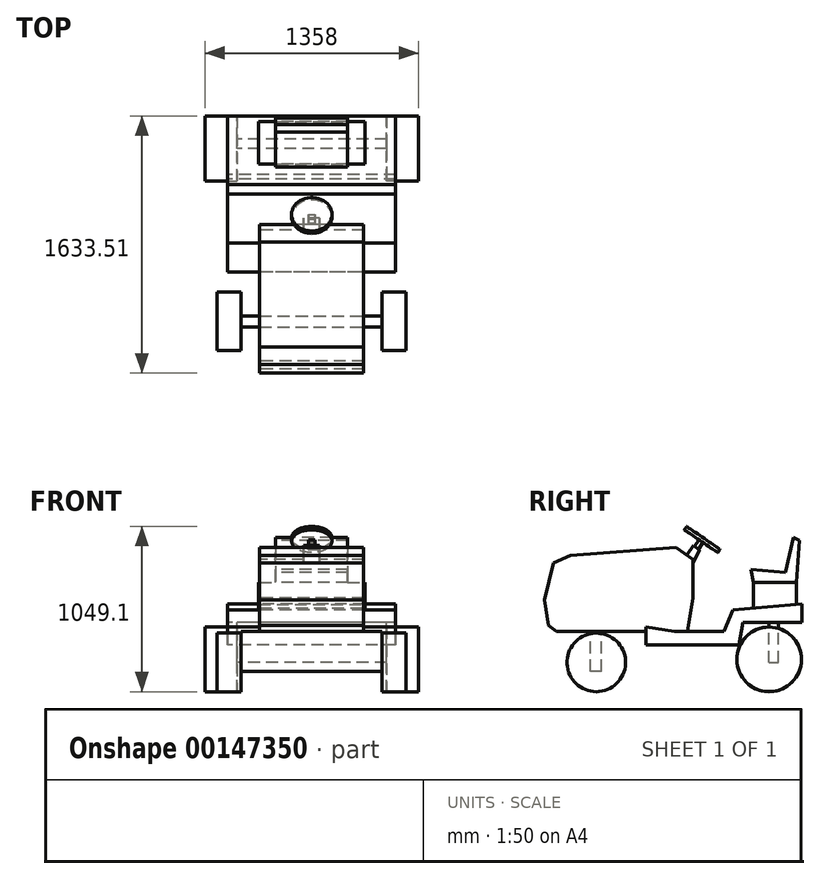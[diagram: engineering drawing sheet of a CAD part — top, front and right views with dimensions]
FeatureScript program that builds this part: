
annotation { "Feature Type Name" : "Feature", "Feature Type Description" : "" }
export const myFeature = defineFeature(function(context is Context, id is Id, definition is map)
    precondition{}
    {
        {
            var Q0;
            Q0=qCreatedBy(makeId("Top.planeOp"),FACE);
            var sketch = newSketch(context, id + "F0", { "sketchPlane" : qUnion([Q0])});
            skLineSegment(sketch, "E0.bottom", {"start": v(-684.79, 956.16) * mm, "end": v(686.81, 956.16) * mm});
            skLineSegment(sketch, "E0.top", {"start": v(-684.79, -771.04) * mm, "end": v(686.81, -771.04) * mm});
            skLineSegment(sketch, "E0.left", {"start": v(-684.79, 956.16) * mm, "end": v(-684.79, -771.04) * mm});
            skLineSegment(sketch, "E0.right", {"start": v(686.81, 956.16) * mm, "end": v(686.81, -771.04) * mm});
            skSolve(sketch);
        }
        {
            var Q0;
            Q0=qCreatedBy(makeId("Right.planeOp"),FACE);
            var sketch = newSketch(context, id + "F1", { "sketchPlane" : qUnion([Q0])});
            skLineSegment(sketch, "E1.bottom", {"start": v(954.63, 0) * mm, "end": v(-771.04, 0) * mm});
            skLineSegment(sketch, "E1.top", {"start": v(954.63, 1041.4) * mm, "end": v(-771.04, 1041.4) * mm});
            skLineSegment(sketch, "E1.left", {"start": v(954.63, 0) * mm, "end": v(954.63, 1041.4) * mm});
            skLineSegment(sketch, "E1.right", {"start": v(-771.04, 0) * mm, "end": v(-771.04, 1041.4) * mm});
            skSolve(sketch);
        }
        {
            var Q0;
            Q0=makeQuery(id+"F1.imprint","IMPRINT",FACE,{"disambiguationData":[TD([[makeQuery(id+"F1.imprint","IMPRINT",EDGE,{"derivedFrom":sQuery(id+"F1.wireOp",EDGE,"E1.bottom")}),-1.0]])]});
            var sketch = newSketch(context, id + "F2", { "sketchPlane" : qUnion([Q0])});
            skLineSegment(sketch, "E2.0", {"start": v(954.63, 438.64) * mm, "end": v(954.63, 557.7) * mm});
            skLineSegment(sketch, "E3", {"start": v(954.63, 557.7) * mm, "end": v(517.3, 520.7) * mm});
            skPoint(sketch, "E3.endSnap0", {"position": v(954.63, 520.7) * mm});
            skLineSegment(sketch, "E4", {"start": v(517.3, 520.7) * mm, "end": v(458.98, 382.76) * mm});
            skLineSegment(sketch, "E5", {"start": v(458.98, 382.76) * mm, "end": v(145.54, 382.76) * mm});
            skLineSegment(sketch, "E6", {"start": v(145.54, 382.76) * mm, "end": v(-36.7, 411.92) * mm});
            skLineSegment(sketch, "E7", {"start": v(-36.7, 411.92) * mm, "end": v(-36.7, 297.72) * mm});
            skLineSegment(sketch, "E8", {"start": v(-36.7, 297.72) * mm, "end": v(553.74, 297.72) * mm});
            skLineSegment(sketch, "E9", {"start": v(553.74, 297.72) * mm, "end": v(580.47, 438.64) * mm});
            skLineSegment(sketch, "E10", {"start": v(580.47, 438.64) * mm, "end": v(954.63, 438.64) * mm});
            skPoint(sketch, "E11.orphan", {"position": v(954.63, 1041.4) * mm});
            skPoint(sketch, "E12.0.end.orphan", {"position": v(-771.04, 1041.4) * mm});
            skPoint(sketch, "E13.0.start.orphan", {"position": v(-771.04, 0) * mm});
            skPoint(sketch, "E14.0.start.orphan", {"position": v(954.63, 0) * mm});
            skSolve(sketch);
        }
        {
            var Q0;
            Q0=qSketchRegion(id+"F2",true);
            extrude(context, id + "F3", {"entities" : qUnion([Q0]), "endBound" : BoundingType.SYMMETRIC, "depth" : 1066.8 * mm});
        }
        {
            var Q0;
            Q0=makeQuery(id+"F1.imprint","IMPRINT",FACE,{"disambiguationData":[TD([[makeQuery(id+"F1.imprint","IMPRINT",EDGE,{"derivedFrom":sQuery(id+"F1.wireOp",EDGE,"E1.bottom")}),-1.0]])]});
            var sketch = newSketch(context, id + "F4", { "sketchPlane" : qUnion([Q0])});
            skLineSegment(sketch, "E15.0", {"start": v(458.98, 382.76) * mm, "end": v(145.54, 382.76) * mm});
            skLineSegment(sketch, "E16", {"start": v(228.74, 382.76) * mm, "end": v(262.65, 594.7) * mm});
            skLineSegment(sketch, "E17", {"start": v(262.65, 594.7) * mm, "end": v(262.65, 840.83) * mm});
            skLineSegment(sketch, "E18", {"start": v(262.65, 840.83) * mm, "end": v(154.41, 914.7) * mm});
            skLineSegment(sketch, "E19", {"start": v(154.41, 914.7) * mm, "end": v(-513.94, 864.88) * mm});
            skLineSegment(sketch, "E20", {"start": v(-513.94, 864.88) * mm, "end": v(-623.9, 818.5) * mm});
            skLineSegment(sketch, "E21", {"start": v(-623.9, 818.5) * mm, "end": v(-678.88, 583.11) * mm});
            skLineSegment(sketch, "E22", {"start": v(-678.88, 583.11) * mm, "end": v(-653.1, 419.89) * mm});
            skLineSegment(sketch, "E23", {"start": v(228.74, 382.76) * mm, "end": v(-603.28, 382.76) * mm});
            skLineSegment(sketch, "E24", {"start": v(-603.28, 382.76) * mm, "end": v(-653.1, 419.89) * mm});
            skPoint(sketch, "E25.0.end.orphan", {"position": v(553.74, 297.72) * mm});
            skPoint(sketch, "E25.0.start.orphan", {"position": v(-36.7, 297.72) * mm});
            skPoint(sketch, "E26.0.end.orphan", {"position": v(-36.7, 411.92) * mm});
            skSolve(sketch);
        }
        {
            var Q0;
            Q0=qSketchRegion(id+"F4",true);
            extrude(context, id + "F5", {"entities" : qUnion([Q0]), "operationType" : NewBodyOperationType.ADD, "endBound" : BoundingType.SYMMETRIC, "depth" : 660.4 * mm});
        }
        {
            var Q0;
            Q0=makeQuery(id+"F5.opExtrude","SWEPT_FACE",FACE,{"disambiguationData":[OSD([sQuery(id+"F4.wireOp",EDGE,"E23")])]});
            var sketch = newSketch(context, id + "F6", { "sketchPlane" : qUnion([Q0])});
            skLineSegment(sketch, "E27.rect.bottom", {"start": v(-447.73, 317.68) * mm, "end": v(447.73, 317.68) * mm});
            skLineSegment(sketch, "E27.rect.top", {"start": v(-447.73, 386.72) * mm, "end": v(447.73, 386.72) * mm});
            skLineSegment(sketch, "E27.rect.left", {"start": v(-447.73, 317.68) * mm, "end": v(-447.73, 386.72) * mm});
            skLineSegment(sketch, "E27.rect.right", {"start": v(447.73, 317.68) * mm, "end": v(447.73, 386.72) * mm});
            skPoint(sketch, "E27.rect.middle", {"position": v(0, 352.2) * mm});
            skSolve(sketch);
        }
        {
            var Q0;
            Q0=qSketchRegion(id+"F6",true);
            extrude(context, id + "F7", {"entities" : qUnion([Q0]), "operationType" : NewBodyOperationType.ADD, "depth" : 254 * mm});
        }
        {
            var Q0;
            Q0=makeQuery(id+"F7.opExtrude","SWEPT_FACE",FACE,{"disambiguationData":[OSD([sQuery(id+"F6.wireOp",EDGE,"E27.rect.left")])]});
            var sketch = newSketch(context, id + "F8", { "sketchPlane" : qUnion([Q0])});
            skLineSegment(sketch, "E28.0", {"start": v(-954.63, 0) * mm, "end": v(771.04, 0) * mm});
            skCircle(sketch, "E29", {"center": v(350.72, 186.22) * mm, "radius": 186.22 * mm});
            skSolve(sketch);
        }
        {
            var Q0;
            Q0=qSketchRegion(id+"F8",true);
            extrude(context, id + "F9", {"entities" : qUnion([Q0]), "depth" : 152.4 * mm});
        }
        {
            var Q0;
            Q0=makeQuery(id+"F9.opExtrude","SWEPT_BODY",BODY,{"disambiguationData":[OSD([sQuery(id+"F8.wireOp",EDGE,"E29")])]});
            var Q1;
            Q1=makeQuery(id+"F1.imprint","IMPRINT",FACE,{"disambiguationData":[TD([[makeQuery(id+"F1.imprint","IMPRINT",EDGE,{"derivedFrom":sQuery(id+"F1.wireOp",EDGE,"E1.bottom")}),-1.0]])]});
            mirror(context, id + "F10", {"operationType" : NewBodyOperationType.ADD, "entities" : qUnion([Q0]), "mirrorPlane" : qUnion([Q1])});
        }
        {
            var Q0;
            Q0=makeQuery(id+"F3.opExtrude","SWEPT_FACE",FACE,{"disambiguationData":[OSD([sQuery(id+"F2.wireOp",EDGE,"E10")])]});
            var sketch = newSketch(context, id + "F11", { "sketchPlane" : qUnion([Q0])});
            skLineSegment(sketch, "E30.rect.bottom", {"start": v(475.8, -747.09) * mm, "end": v(-475.8, -747.09) * mm});
            skLineSegment(sketch, "E30.rect.top", {"start": v(475.8, -805.5) * mm, "end": v(-475.8, -805.5) * mm});
            skLineSegment(sketch, "E30.rect.left", {"start": v(475.8, -747.09) * mm, "end": v(475.8, -805.5) * mm});
            skLineSegment(sketch, "E30.rect.right", {"start": v(-475.8, -747.09) * mm, "end": v(-475.8, -805.5) * mm});
            skPoint(sketch, "E30.rect.middle", {"position": v(0, -776.3) * mm});
            skPoint(sketch, "E31.orphan", {"position": v(0, -954.63) * mm});
            skSolve(sketch);
        }
        {
            var Q0;
            Q0=qSketchRegion(id+"F11",true);
            extrude(context, id + "F12", {"entities" : qUnion([Q0]), "operationType" : NewBodyOperationType.ADD, "depth" : 254 * mm});
        }
        {
            var Q0;
            Q0=makeQuery(id+"F12.opExtrude","SWEPT_FACE",FACE,{"disambiguationData":[OSD([sQuery(id+"F11.wireOp",EDGE,"E30.rect.right")])]});
            var sketch = newSketch(context, id + "F13", { "sketchPlane" : qUnion([Q0])});
            skCircle(sketch, "E32", {"center": v(-747.09, 205.12) * mm, "radius": 205.12 * mm});
            skPoint(sketch, "E32.centerSnap0", {"position": v(-747.09, 184.64) * mm});
            skSolve(sketch);
        }
        {
            var Q0;
            Q0=qSketchRegion(id+"F13",true);
            extrude(context, id + "F14", {"entities" : qUnion([Q0]), "operationType" : NewBodyOperationType.ADD, "depth" : 203.2 * mm});
        }
        {
            var Q0;
            Q0=makeQuery(id+"F12.opExtrude","SWEPT_FACE",FACE,{"disambiguationData":[OSD([sQuery(id+"F11.wireOp",EDGE,"E30.rect.left")])]});
            var sketch = newSketch(context, id + "F15", { "sketchPlane" : qUnion([Q0])});
            skCircle(sketch, "E33", {"center": v(747.09, 205.12) * mm, "radius": 205.12 * mm});
            skArc(sketch, "E34.0", {"start": v(805.5, 401.75) * mm, "mid": v(717.57, 2.13) * mm, "end": v(747.09, 410.25) * mm});
            skSolve(sketch);
        }
        {
            var Q0;
            Q0=qSketchRegion(id+"F15",true);
            extrude(context, id + "F16", {"entities" : qUnion([Q0]), "operationType" : NewBodyOperationType.ADD, "depth" : 203.2 * mm});
        }
        {
            var Q0;
            Q0=makeQuery(id+"F3.opExtrude","SWEPT_FACE",FACE,{"disambiguationData":[OSD([sQuery(id+"F2.wireOp",EDGE,"E10")])]});
            var sketch = newSketch(context, id + "F17", { "sketchPlane" : qUnion([Q0])});
            skLineSegment(sketch, "E35.rect.bottom", {"start": v(-336.71, -648.84) * mm, "end": v(336.71, -648.84) * mm});
            skLineSegment(sketch, "E35.rect.top", {"start": v(-336.71, -919.68) * mm, "end": v(336.71, -919.68) * mm});
            skLineSegment(sketch, "E35.rect.left", {"start": v(-336.71, -648.84) * mm, "end": v(-336.71, -919.68) * mm});
            skLineSegment(sketch, "E35.rect.right", {"start": v(336.71, -648.84) * mm, "end": v(336.71, -919.68) * mm});
            skPoint(sketch, "E35.rect.middle", {"position": v(0, -784.26) * mm});
            skPoint(sketch, "E35.rect.middle.positionSnap0", {"position": v(0, -747.09) * mm});
            skPoint(sketch, "E35.rect.centerSnap0", {"position": v(0, -747.09) * mm});
            skSolve(sketch);
        }
        {
            var Q0;
            Q0=qSketchRegion(id+"F17",true);
            extrude(context, id + "F18", {"entities" : qUnion([Q0]), "operationType" : NewBodyOperationType.ADD, "oppositeDirection" : true, "depth" : 254 * mm});
        }
        {
            var Q0;
            Q0=makeQuery(id+"F1.imprint","IMPRINT",FACE,{"disambiguationData":[TD([[makeQuery(id+"F1.imprint","IMPRINT",EDGE,{"derivedFrom":sQuery(id+"F1.wireOp",EDGE,"E1.bottom")}),-1.0]])]});
            var sketch = newSketch(context, id + "F19", { "sketchPlane" : qUnion([Q0])});
            skLineSegment(sketch, "E36.0", {"start": v(648.84, 692.64) * mm, "end": v(919.68, 692.64) * mm});
            skLineSegment(sketch, "E37", {"start": v(919.68, 692.64) * mm, "end": v(939.6, 959.61) * mm});
            skLineSegment(sketch, "E38", {"start": v(939.6, 959.61) * mm, "end": v(900.08, 978.5) * mm});
            skLineSegment(sketch, "E39", {"start": v(900.08, 978.5) * mm, "end": v(850.25, 758.59) * mm});
            skLineSegment(sketch, "E40", {"start": v(850.25, 758.59) * mm, "end": v(630.33, 775.77) * mm});
            skLineSegment(sketch, "E41", {"start": v(630.33, 775.77) * mm, "end": v(648.84, 692.64) * mm});
            skSolve(sketch);
        }
        {
            var Q0;
            Q0=qSketchRegion(id+"F19",true);
            extrude(context, id + "F20", {"entities" : qUnion([Q0]), "operationType" : NewBodyOperationType.ADD, "endBound" : BoundingType.SYMMETRIC, "depth" : 457.2 * mm});
        }
        {
            var Q0;
            Q0=makeQuery(id+"F1.imprint","IMPRINT",FACE,{"disambiguationData":[TD([[makeQuery(id+"F1.imprint","IMPRINT",EDGE,{"derivedFrom":sQuery(id+"F1.wireOp",EDGE,"E1.bottom")}),-1.0]])]});
            var sketch = newSketch(context, id + "F21", { "sketchPlane" : qUnion([Q0])});
            skLineSegment(sketch, "E42.0", {"start": v(262.65, 840.83) * mm, "end": v(224.07, 867.17) * mm});
            skLineSegment(sketch, "E43.0", {"start": v(262.65, 813.34) * mm, "end": v(262.65, 840.83) * mm});
            skLineSegment(sketch, "E44", {"start": v(224.07, 867.17) * mm, "end": v(265.45, 927.8) * mm});
            skLineSegment(sketch, "E45", {"start": v(265.45, 927.8) * mm, "end": v(304.6, 901.08) * mm});
            skLineSegment(sketch, "E46", {"start": v(304.6, 901.08) * mm, "end": v(262.65, 813.34) * mm});
            skPoint(sketch, "E47.orphan", {"position": v(262.65, 594.7) * mm});
            skPoint(sketch, "E48.orphan", {"position": v(154.41, 914.7) * mm});
            skSolve(sketch);
        }
        {
            var Q0;
            Q0=qSketchRegion(id+"F21",true);
            extrude(context, id + "F22", {"entities" : qUnion([Q0]), "operationType" : NewBodyOperationType.ADD, "endBound" : BoundingType.SYMMETRIC, "depth" : 101.6 * mm});
        }
        {
            var Q0;
            Q0=makeQuery(id+"F22.opExtrude","SWEPT_FACE",FACE,{"disambiguationData":[OSD([sQuery(id+"F21.wireOp",EDGE,"E45")])]});
            var sketch = newSketch(context, id + "F23", { "sketchPlane" : qUnion([Q0])});
            skLineSegment(sketch, "E49.rect.bottom", {"start": v(-19.95, -294.88) * mm, "end": v(19.95, -294.88) * mm});
            skLineSegment(sketch, "E49.rect.top", {"start": v(-19.95, -262.9) * mm, "end": v(19.95, -262.9) * mm});
            skLineSegment(sketch, "E49.rect.left", {"start": v(-19.95, -294.88) * mm, "end": v(-19.95, -262.9) * mm});
            skLineSegment(sketch, "E49.rect.right", {"start": v(19.95, -294.88) * mm, "end": v(19.95, -262.9) * mm});
            skPoint(sketch, "E49.rect.middle", {"position": v(0, -278.9) * mm});
            skSolve(sketch);
        }
        {
            var Q0;
            Q0=qSketchRegion(id+"F23",true);
            extrude(context, id + "F24", {"entities" : qUnion([Q0]), "operationType" : NewBodyOperationType.ADD, "depth" : 50.8 * mm});
        }
        {
            var Q0;
            Q0=makeQuery(id+"F24.opExtrude","CAP_FACE",FACE,{"disambiguationData":[OSD([sQuery(id+"F23.wireOp",EDGE,"E49.rect.bottom"),sQuery(id+"F23.wireOp",EDGE,"E49.rect.top"),sQuery(id+"F23.wireOp",EDGE,"E49.rect.left"),sQuery(id+"F23.wireOp",EDGE,"E49.rect.right")])],"isStart":false});
            var sketch = newSketch(context, id + "F25", { "sketchPlane" : qUnion([Q0])});
            skCircle(sketch, "E50", {"center": v(0, -278.9) * mm, "radius": 128.43 * mm});
            skSolve(sketch);
        }
        {
            var Q0;
            Q0=qSketchRegion(id+"F25",true);
            extrude(context, id + "F26", {"entities" : qUnion([Q0]), "operationType" : NewBodyOperationType.ADD, "depth" : 25.4 * mm});
        }
    });
